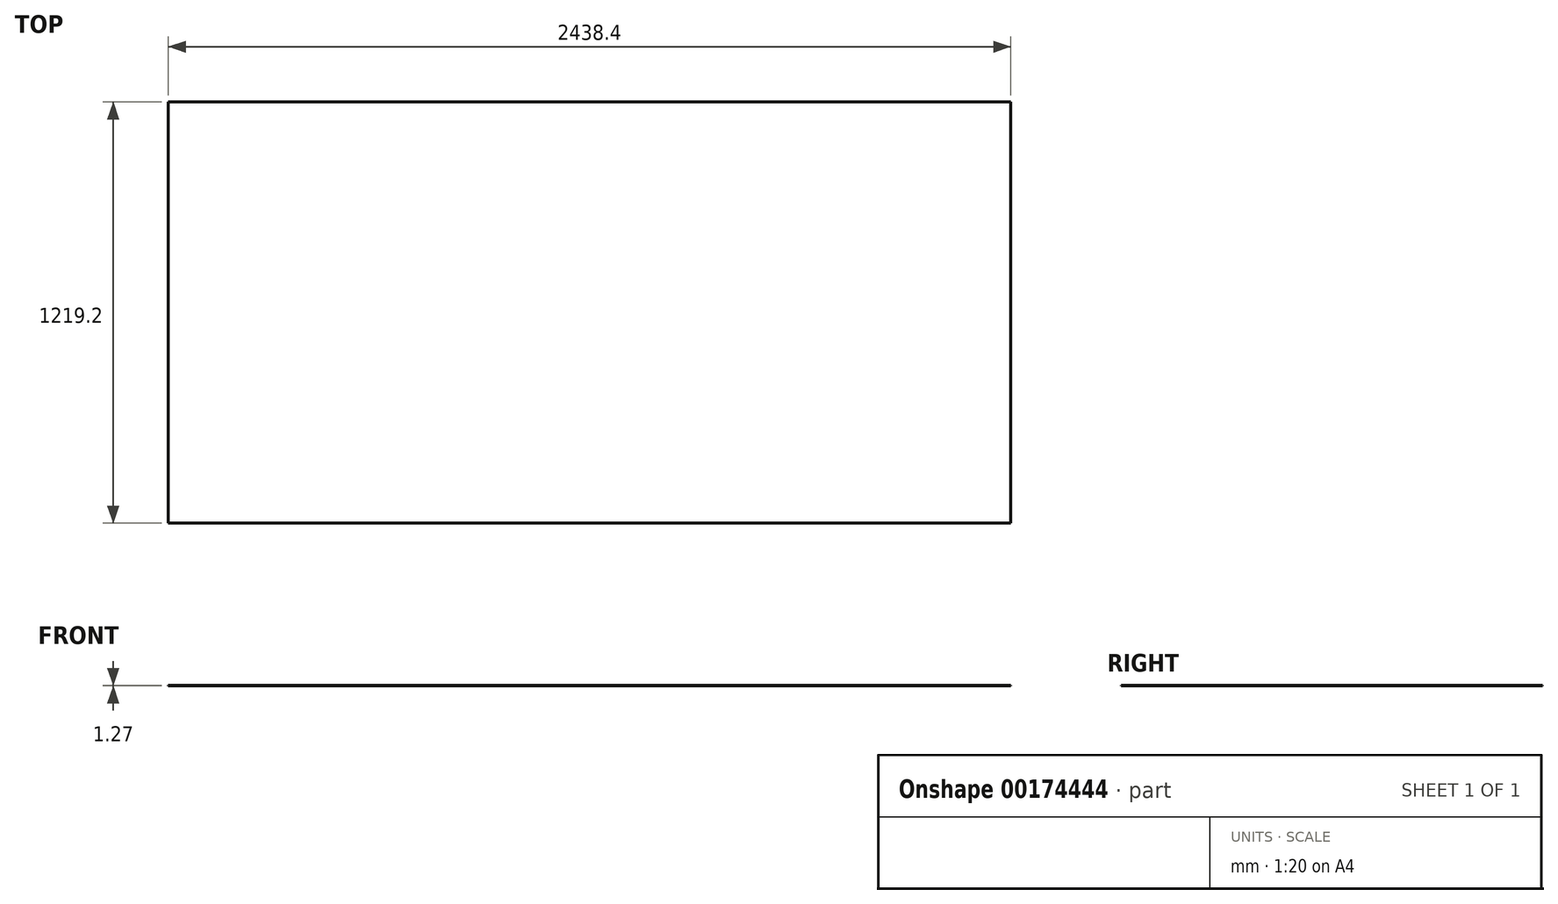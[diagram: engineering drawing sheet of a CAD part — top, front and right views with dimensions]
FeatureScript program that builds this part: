
annotation { "Feature Type Name" : "Feature", "Feature Type Description" : "" }
export const myFeature = defineFeature(function(context is Context, id is Id, definition is map)
    precondition{}
    {
        {
            var Q0;
            Q0=qCreatedBy(makeId("Top.planeOp"),FACE);
            var sketch = newSketch(context, id + "F0", { "sketchPlane" : qUnion([Q0])});
            skLineSegment(sketch, "E0.bottom", {"start": v(0, 0) * mm, "end": v(2438.4, 0) * mm});
            skLineSegment(sketch, "E0.top", {"start": v(0, 1219.2) * mm, "end": v(2438.4, 1219.2) * mm});
            skLineSegment(sketch, "E0.left", {"start": v(0, 0) * mm, "end": v(0, 1219.2) * mm});
            skLineSegment(sketch, "E0.right", {"start": v(2438.4, 0) * mm, "end": v(2438.4, 1219.2) * mm});
            skSolve(sketch);
        }
        {
            var Q0;
            Q0 = qSketchRegion(id + "F0", true);
            extrude(context, id + "F1", {"entities" : qUnion([Q0]), "oppositeDirection" : true, "depth" : 1.27 * mm});
        }
    });
